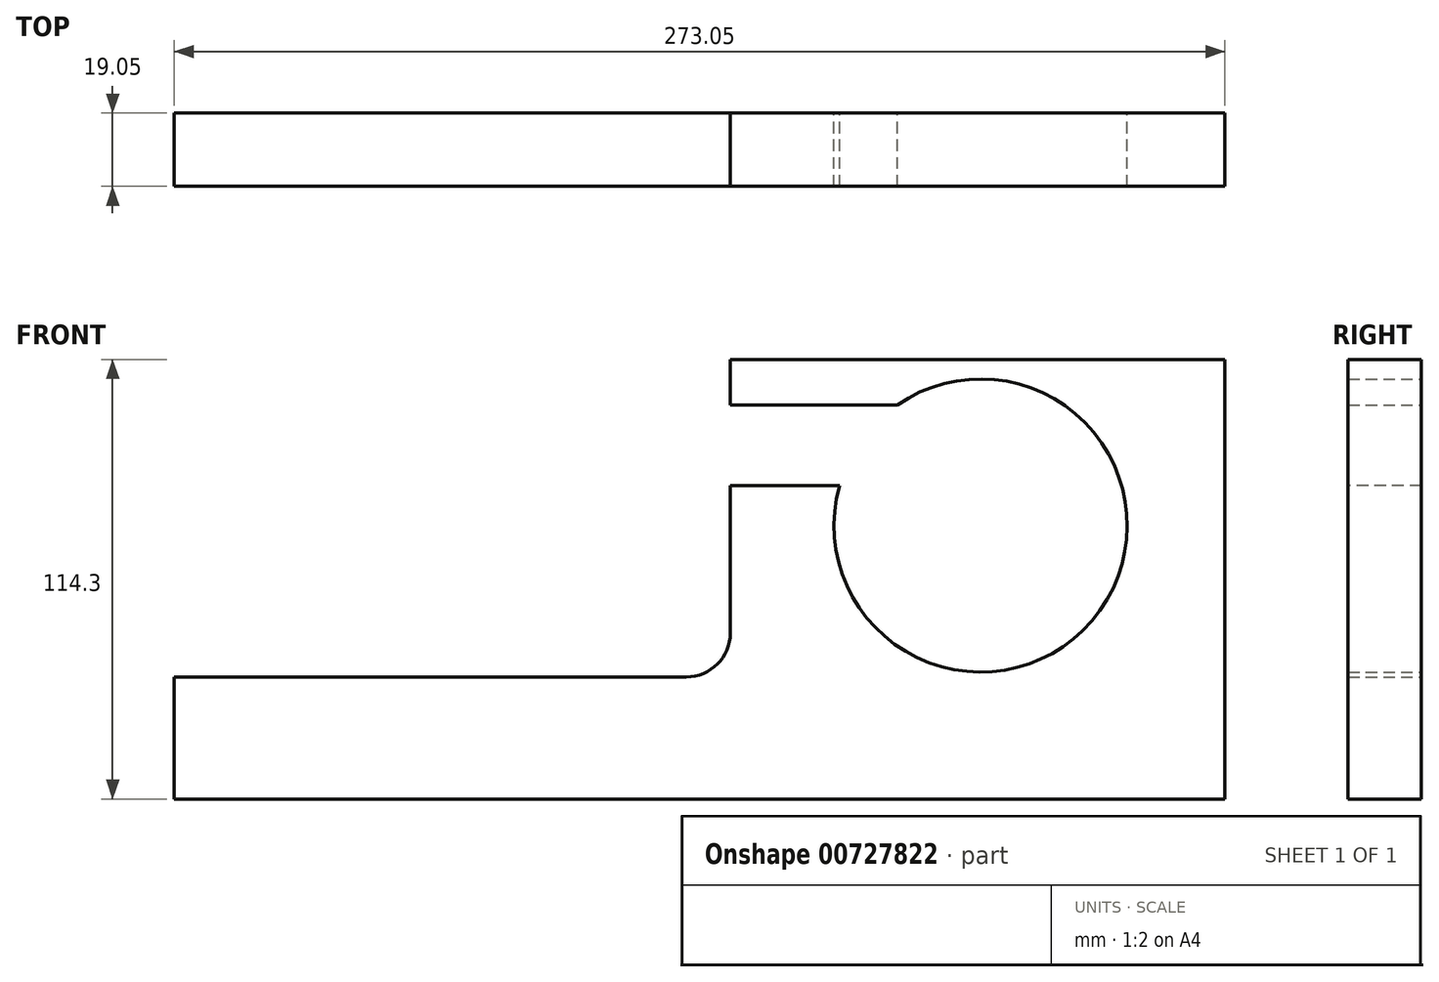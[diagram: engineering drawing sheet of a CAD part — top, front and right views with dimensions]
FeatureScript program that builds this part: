
annotation { "Feature Type Name" : "Feature", "Feature Type Description" : "" }
export const myFeature = defineFeature(function(context is Context, id is Id, definition is map)
    precondition{}
    {
        {
            var Q0;
            Q0=qCreatedBy(makeId("Front.planeOp"),FACE);
            var sketch = newSketch(context, id + "F0", { "sketchPlane" : qUnion([Q0])});
            skLineSegment(sketch, "E0.bottom", {"start": v(0, 0) * mm, "end": v(273.05, 0) * mm});
            skLineSegment(sketch, "E0.top", {"start": v(0, 114.3) * mm, "end": v(273.05, 114.3) * mm});
            skLineSegment(sketch, "E0.left", {"start": v(0, 0) * mm, "end": v(0, 114.3) * mm});
            skLineSegment(sketch, "E0.right", {"start": v(273.05, 0) * mm, "end": v(273.05, 114.3) * mm});
            skSolve(sketch);
        }
        {
            var Q0;
            Q0=makeQuery(id+"F0.imprint","IMPRINT",FACE,{"disambiguationData":[TD([[makeQuery(id+"F0.imprint","IMPRINT",EDGE,{"derivedFrom":sQuery(id+"F0.wireOp",EDGE,"E0.bottom")}),1.0]])]});
            extrude(context, id + "F1", {"entities" : qUnion([Q0]), "depth" : 19.05 * mm, "offsetDistance" : 25.4 * mm});
        }
        {
            var Q0;
            Q0=qCreatedBy(makeId("Front.planeOp"),FACE);
            var sketch = newSketch(context, id + "F2", { "sketchPlane" : qUnion([Q0])});
            skLineSegment(sketch, "E1", {"start": v(0, 114.3) * mm, "end": v(0, 31.75) * mm});
            skLineSegment(sketch, "E2", {"start": v(0, 31.75) * mm, "end": v(133.09, 31.75) * mm});
            skLineSegment(sketch, "E3", {"start": v(144.52, 43.18) * mm, "end": v(144.52, 82.55) * mm});
            skLineSegment(sketch, "E4", {"start": v(144.52, 82.55) * mm, "end": v(157.22, 82.55) * mm});
            skLineSegment(sketch, "E5", {"start": v(157.22, 82.55) * mm, "end": v(157.22, 102.34) * mm});
            skLineSegment(sketch, "E6", {"start": v(157.22, 102.34) * mm, "end": v(144.52, 102.34) * mm});
            skLineSegment(sketch, "E7", {"start": v(144.52, 102.34) * mm, "end": v(144.52, 115.04) * mm});
            skLineSegment(sketch, "E8", {"start": v(144.52, 115.04) * mm, "end": v(0, 114.3) * mm});
            skPoint(sketch, "E9.visualSharp", {"position": v(144.52, 31.75) * mm});
            skArc(sketch, "E9.filletArc", {"start": v(133.09, 31.75) * mm, "mid": v(141.17, 35.1) * mm, "end": v(144.52, 43.18) * mm});
            skSolve(sketch);
        }
        {
            var Q0;
            Q0 = qSketchRegion(id + "F2", true);
            extrude(context, id + "F3", {"entities" : qUnion([Q0]), "operationType" : NewBodyOperationType.REMOVE, "depth" : 25.4 * mm, "offsetDistance" : 25.4 * mm});
        }
        {
            var Q0;
            Q0=qCreatedBy(makeId("Front.planeOp"),FACE);
            var sketch = newSketch(context, id + "F4", { "sketchPlane" : qUnion([Q0])});
            skCircle(sketch, "E10", {"center": v(209.55, 71.12) * mm, "radius": 38.1 * mm});
            skLineSegment(sketch, "E11", {"start": v(156.64, 102.46) * mm, "end": v(192.52, 102.46) * mm});
            skLineSegment(sketch, "E12", {"start": v(192.52, 102.46) * mm, "end": v(192.52, 81.46) * mm});
            skLineSegment(sketch, "E13", {"start": v(192.52, 81.46) * mm, "end": v(144.04, 81.46) * mm});
            skLineSegment(sketch, "E14", {"start": v(144.04, 81.46) * mm, "end": v(144.04, 102.46) * mm});
            skLineSegment(sketch, "E15", {"start": v(144.04, 102.46) * mm, "end": v(156.64, 102.46) * mm});
            skLineSegment(sketch, "E16", {"start": v(144.36, 113.83) * mm, "end": v(207.86, 113.83) * mm});
            skLineSegment(sketch, "E17", {"start": v(207.86, 113.83) * mm, "end": v(209.55, 71.12) * mm});
            skSolve(sketch);
        }
        {
            var Q0;
            Q0 = qSketchRegion(id + "F4", true);
            extrude(context, id + "F5", {"entities" : qUnion([Q0]), "operationType" : NewBodyOperationType.REMOVE, "depth" : 25.4 * mm, "offsetDistance" : 25.4 * mm});
        }
    });
